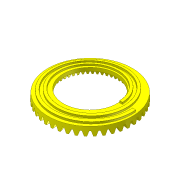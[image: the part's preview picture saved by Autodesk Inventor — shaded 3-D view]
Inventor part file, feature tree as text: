
AUTODESK INVENTOR PART (.ipt)
format: ipt  version: 2016 (Build 200138000, 138)  size: 501,760 bytes
history: native  units: in
note: dims shown in document units (in); Inventor stores cm internally (conversion verified against a paired STEP export)
features: sketch x5, plane x3, other x2, fillet x2, revolve x1, helix x1, extrude x1, loft x1, pattern_circular x1
ambient origin geometry x8: Origin, YZ Plane, XZ Plane, XY Plane, X Axis, Y Axis, Z Axis, Center Point
bodies: Solid1 (feature_tree)
feature tree (17):
  revolve  "Revolution3"  [1 undecoded]
  other  "Work Point1"
  plane  "Work Plane7"
  sketch  "Sketch12"  dims[d90=0.065in d91=0.2756in d92=0.0394in d96=0.0492in]
  helix  "Coil1"  [1 undecoded]
  extrude  "Extrusion8"  Depth=0.2756in
  other  "Work Axis1"
  fillet  "Fillet3"  Radius=0.0394in
  fillet  "Fillet4"  Radius=0.0492in
  plane  "Work Plane9"
  loft  "Loft1"
  pattern_circular  "Circular Pattern3"  [2 undecoded]
  sketch  "Sketch1"  dims[d1=0.1825in d88=0.1575in d89=0.0852in]
  sketch  "Sketch13"  dims[d97=0.2756in d98=0.1969in]
  sketch  "Sketch14"  dims[d99=90.0deg]
  plane  "Work Plane8"
  sketch  "Sketch15"  dims[d101=0.9449in d102=0.1575in d103=1.8898in d104=0.6299in d105=0.0591in d106=0.0394in d107=0.1181in d108=0.3937in d109=0.7874in d110=0.0in d111=90.0deg d112=90.0deg d113=0.0in d114=0.0in d115=1.1811in d116=0.3937in d117=0.0in d118=0.002in d119=0.002in d120=0.9579in d121=0.5534in d122=0.9646in d123=0.0394in d124=0.0886in d125=0.1374in d126=0.0309in d127=0.0079in d128=0.0in d129=90.0deg d130=0.0in d131=90.0deg d132=18.8976in d133=360.0deg]
note: 4 required parameter values undecoded (feature->parameter linkage not recoverable at this tier; creation-order binding heuristic only, values carry confidence <= 0.55)